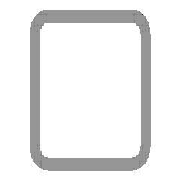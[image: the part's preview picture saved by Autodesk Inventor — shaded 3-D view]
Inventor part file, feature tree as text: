
AUTODESK INVENTOR PART (.ipt)
format: ipt  version: 2017 (Build 210142000, 142)  size: 133,632 bytes
history: native  units: mm (DEFAULTED — no unit token found)
features: other x4, plane x3, sketch x3, split x2
ambient origin geometry x8: Origin, YZ Plane, XZ Plane, XY Plane, X Axis, Y Axis, Z Axis, Center Point
bodies: Solid1 (feature_tree), Body (feature_tree)
feature tree (12):
  parser-record x1  (decoder bookkeeping rows leaked as tree rows — omitted from the tree; the rows remain in map.json)
  other  "Driven Length"
  other  "Start plane"
  other  "End plane"
  plane  "Work Plane4"
  split  "Split1"
  plane  "Work Plane5"
  split  "Split2"
  sketch  "Sketch"  dims[d10=76.2mm d11=76.2mm d12=6.35mm d13=203.2mm d14=889.0mm d15=38.1mm d16=38.1mm d17=12.7mm d18=90.0deg d19=685.8mm]
  sketch  "Sketch3"  dims[d3=685.8mm]
  plane  "Work Plane3"
  sketch  "Sketch4"  dims[d4=0.0mm]
